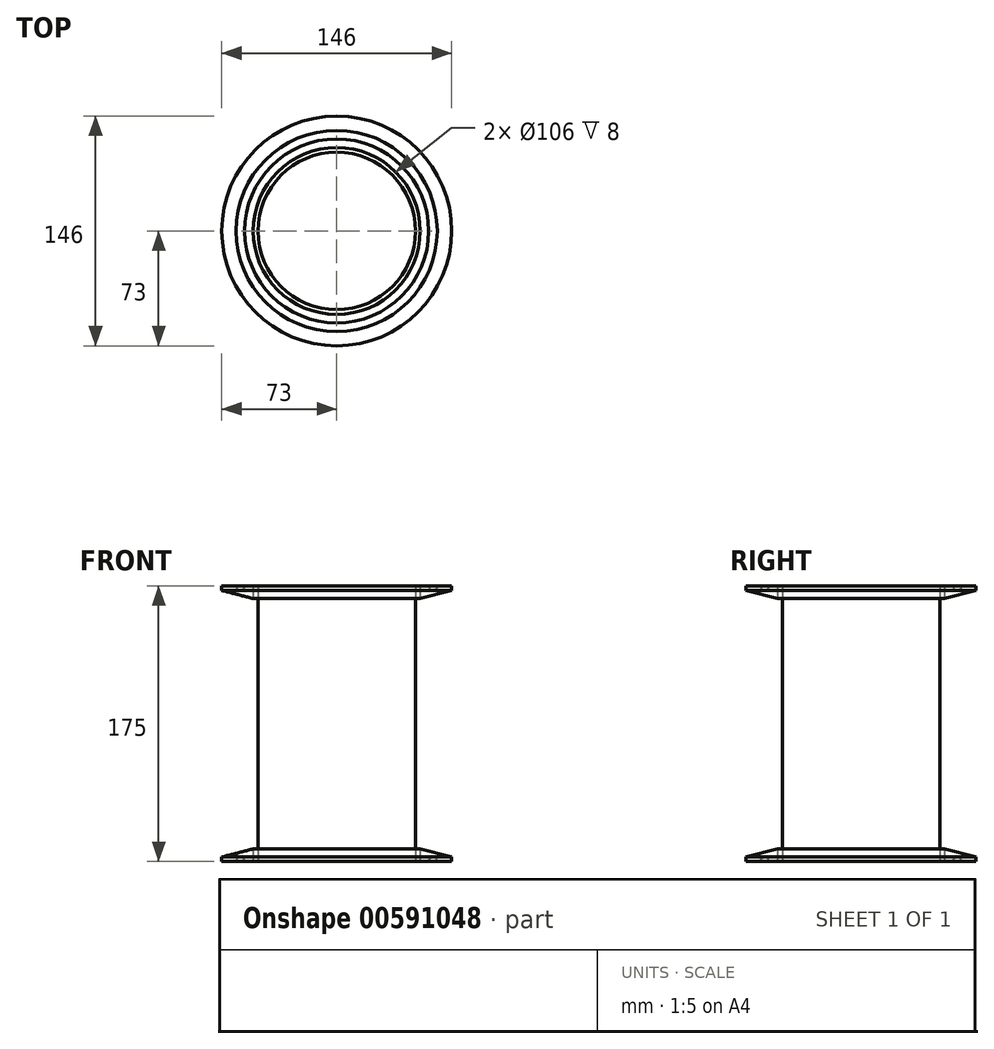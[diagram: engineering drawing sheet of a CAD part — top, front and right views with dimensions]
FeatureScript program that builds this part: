
annotation { "Feature Type Name" : "Feature", "Feature Type Description" : "" }
export const myFeature = defineFeature(function(context is Context, id is Id, definition is map)
    precondition{}
    {
        {
            var Q0;
            Q0=qCreatedBy(makeId("Front.planeOp"),FACE);
            var sketch = newSketch(context, id + "F0", { "sketchPlane" : qUnion([Q0])});
            skLineSegment(sketch, "E0", {"start": v(0, 0) * mm, "end": v(-53, 0) * mm});
            skLineSegment(sketch, "E1", {"start": v(-53, 0) * mm, "end": v(-73, 0) * mm});
            skLineSegment(sketch, "E2", {"start": v(-53, 0) * mm, "end": v(-53, 8) * mm});
            skLineSegment(sketch, "E3", {"start": v(-53, 8) * mm, "end": v(-73, 2.82) * mm});
            skLineSegment(sketch, "E4", {"start": v(-73, 2.82) * mm, "end": v(-73, 0) * mm});
            skLineSegment(sketch, "E5", {"start": v(-53, 8) * mm, "end": v(-53, 87.5) * mm});
            skLineSegment(sketch, "E6", {"start": v(-53, 87.5) * mm, "end": v(0, 87.5) * mm, "construction": true});
            skLineSegment(sketch, "E7", {"start": v(0, 87.5) * mm, "end": v(0, 0) * mm});
            skLineSegment(sketch, "E8", {"start": v(0, 0) * mm, "end": v(-50, 0) * mm});
            skLineSegment(sketch, "E9", {"start": v(-50, 0) * mm, "end": v(-50, 87.5) * mm});
            skCircle(sketch, "E10", {"center": v(-61.16, 0) * mm, "radius": 2.72 * mm});
            skLineSegment(sketch, "E11.MirrorCS", {"start": v(-73, 172.18) * mm, "end": v(-73, 175) * mm});
            skLineSegment(sketch, "E12.MirrorCS", {"start": v(0, 175) * mm, "end": v(-53, 175) * mm});
            skLineSegment(sketch, "E13.MirrorCS", {"start": v(-53, 175) * mm, "end": v(-53, 167) * mm});
            skLineSegment(sketch, "E14.MirrorCS", {"start": v(0, 175) * mm, "end": v(-50, 175) * mm});
            skLineSegment(sketch, "E15.MirrorCS", {"start": v(-53, 175) * mm, "end": v(-73, 175) * mm});
            skCircle(sketch, "E16.MirrorC", {"center": v(-61.16, 175) * mm, "radius": 2.72 * mm});
            skLineSegment(sketch, "E17.MirrorCS", {"start": v(0, 87.5) * mm, "end": v(0, 175) * mm});
            skLineSegment(sketch, "E18.MirrorCS", {"start": v(-53, 167) * mm, "end": v(-73, 172.18) * mm});
            skLineSegment(sketch, "E19.MirrorCS", {"start": v(-53, 167) * mm, "end": v(-53, 87.5) * mm});
            skLineSegment(sketch, "E20.MirrorCS", {"start": v(-50, 175) * mm, "end": v(-50, 87.5) * mm});
            skSolve(sketch);
        }
        {
            var Q0;
            {var subQ0=sQuery(id+"F0.wireOp",EDGE,"E2");Q0=makeQuery(id+"F0.imprint","IMPRINT",FACE,{"disambiguationData":[TD([[makeQuery(id+"F0.imprint","IMPRINT",EDGE,{"derivedFrom":subQ0}),1.0]])]});}
            var Q1;
            {var subQ4=sQuery(id+"F0.wireOp",EDGE,"E13.MirrorCS");Q1=makeQuery(id+"F0.imprint","IMPRINT",FACE,{"disambiguationData":[TD([[makeQuery(id+"F0.imprint","IMPRINT",EDGE,{"derivedFrom":subQ4}),-1.0]])]});}
            var Q2;
            Q2=makeQuery(id+"F0.imprint","IMPRINT",FACE,{"disambiguationData":[TD([[makeQuery(id+"F0.imprint","IMPRINT",EDGE,{"derivedFrom":sQuery(id+"F0.wireOp",EDGE,"E0")}),-1.0]])]});
            var Q3;
            Q3=sQuery(id+"F0.wireOp",EDGE,"E17.MirrorCS");
            revolve(context, id + "F1", {"entities" : qUnion([Q0, Q1, Q2]), "axis" : qUnion([Q3]), "revolveType" : RevolveType.FULL});
        }
    });
